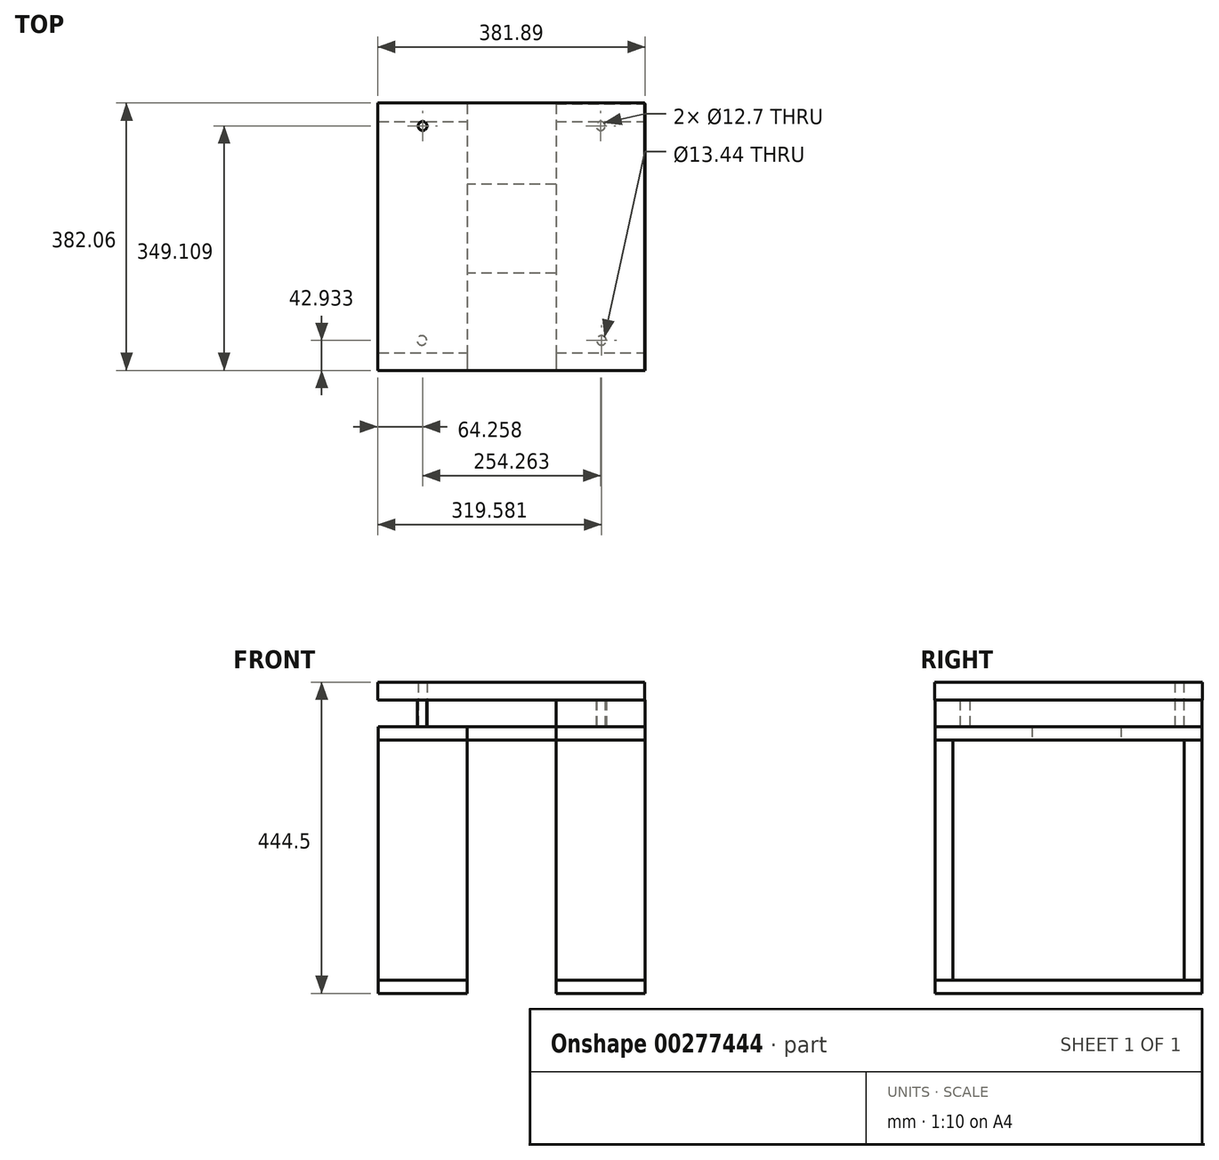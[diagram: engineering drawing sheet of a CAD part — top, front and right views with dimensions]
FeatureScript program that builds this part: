
annotation { "Feature Type Name" : "Feature", "Feature Type Description" : "" }
export const myFeature = defineFeature(function(context is Context, id is Id, definition is map)
    precondition{}
    {
        {
            var Q0;
            Q0=qCreatedBy(makeId("Top.planeOp"),FACE);
            var sketch = newSketch(context, id + "F0", { "sketchPlane" : qUnion([Q0])});
            skLineSegment(sketch, "E0.bottom", {"start": v(63.5, 136.92) * mm, "end": v(190.5, 136.92) * mm});
            skLineSegment(sketch, "E0.top", {"start": v(63.5, -244.08) * mm, "end": v(190.5, -244.08) * mm});
            skLineSegment(sketch, "E0.left", {"start": v(63.5, 136.92) * mm, "end": v(63.5, -244.08) * mm});
            skLineSegment(sketch, "E0.right", {"start": v(190.5, 136.92) * mm, "end": v(190.5, -244.08) * mm});
            skLineSegment(sketch, "E1", {"start": v(0, 353.22) * mm, "end": v(0, -367.1) * mm});
            skLineSegment(sketch, "E2.MirrorCS", {"start": v(-190.5, 136.92) * mm, "end": v(-190.5, -244.08) * mm});
            skLineSegment(sketch, "E3.MirrorCS", {"start": v(-63.5, 136.92) * mm, "end": v(-190.5, 136.92) * mm});
            skLineSegment(sketch, "E4.MirrorCS", {"start": v(-63.5, 136.92) * mm, "end": v(-63.5, -244.08) * mm});
            skLineSegment(sketch, "E5.MirrorCS", {"start": v(-63.5, -244.08) * mm, "end": v(-190.5, -244.08) * mm});
            skSolve(sketch);
        }
        {
            var Q0;
            Q0=makeQuery(id+"F0.imprint","IMPRINT",FACE,{"disambiguationData":[TD([[makeQuery(id+"F0.imprint","IMPRINT",EDGE,{"derivedFrom":sQuery(id+"F0.wireOp",EDGE,"E2.MirrorCS")}),1.0]])]});
            var Q1;
            Q1=makeQuery(id+"F0.imprint","IMPRINT",FACE,{"disambiguationData":[TD([[makeQuery(id+"F0.imprint","IMPRINT",EDGE,{"derivedFrom":sQuery(id+"F0.wireOp",EDGE,"E0.bottom")}),-1.0]])]});
            extrude(context, id + "F1", {"entities" : qUnion([Q0, Q1]), "depth" : 19.05 * mm});
        }
        {
            var Q0;
            Q0=makeQuery(id+"F1.opExtrude","CAP_FACE",FACE,{"disambiguationData":[OSD([sQuery(id+"F0.wireOp",EDGE,"E2.MirrorCS"),sQuery(id+"F0.wireOp",EDGE,"E3.MirrorCS"),sQuery(id+"F0.wireOp",EDGE,"E4.MirrorCS"),sQuery(id+"F0.wireOp",EDGE,"E5.MirrorCS")])],"isStart":false});
            var sketch = newSketch(context, id + "F2", { "sketchPlane" : qUnion([Q0])});
            skLineSegment(sketch, "E6.bottom", {"start": v(-190.5, 136.92) * mm, "end": v(-63.5, 136.92) * mm});
            skLineSegment(sketch, "E6.top", {"start": v(-190.5, 111.52) * mm, "end": v(-63.5, 111.52) * mm});
            skLineSegment(sketch, "E6.left", {"start": v(-190.5, 136.92) * mm, "end": v(-190.5, 111.52) * mm});
            skLineSegment(sketch, "E6.right", {"start": v(-63.5, 136.92) * mm, "end": v(-63.5, 111.52) * mm});
            skLineSegment(sketch, "E7.bottom", {"start": v(63.15, 136.92) * mm, "end": v(190.15, 136.92) * mm});
            skLineSegment(sketch, "E7.top", {"start": v(63.15, 111.52) * mm, "end": v(190.15, 111.52) * mm});
            skLineSegment(sketch, "E7.left", {"start": v(63.15, 136.92) * mm, "end": v(63.15, 111.52) * mm});
            skLineSegment(sketch, "E7.right", {"start": v(190.15, 136.92) * mm, "end": v(190.15, 111.52) * mm});
            skLineSegment(sketch, "E8.bottom", {"start": v(-190.5, -218.68) * mm, "end": v(-63.5, -218.68) * mm});
            skLineSegment(sketch, "E8.top", {"start": v(-190.5, -244.08) * mm, "end": v(-63.5, -244.08) * mm});
            skLineSegment(sketch, "E8.left", {"start": v(-190.5, -218.68) * mm, "end": v(-190.5, -244.08) * mm});
            skLineSegment(sketch, "E8.right", {"start": v(-63.5, -218.68) * mm, "end": v(-63.5, -244.08) * mm});
            skLineSegment(sketch, "E9.bottom", {"start": v(63.15, -218.68) * mm, "end": v(190.15, -218.68) * mm});
            skLineSegment(sketch, "E9.top", {"start": v(63.15, -244.08) * mm, "end": v(190.15, -244.08) * mm});
            skLineSegment(sketch, "E9.left", {"start": v(63.15, -218.68) * mm, "end": v(63.15, -244.08) * mm});
            skLineSegment(sketch, "E9.right", {"start": v(190.15, -218.68) * mm, "end": v(190.15, -244.08) * mm});
            skSolve(sketch);
        }
        {
            var Q0;
            Q0=makeQuery(id+"F2.imprint","IMPRINT",FACE,{"disambiguationData":[TD([[makeQuery(id+"F2.imprint","IMPRINT",EDGE,{"derivedFrom":sQuery(id+"F2.wireOp",EDGE,"E6.bottom")}),1.0]])]});
            var Q1;
            Q1=makeQuery(id+"F2.imprint","IMPRINT",FACE,{"disambiguationData":[TD([[makeQuery(id+"F2.imprint","IMPRINT",EDGE,{"derivedFrom":sQuery(id+"F2.wireOp",EDGE,"E7.bottom")}),-1.0]])]});
            var Q2;
            Q2=makeQuery(id+"F2.imprint","IMPRINT",FACE,{"disambiguationData":[TD([[makeQuery(id+"F2.imprint","IMPRINT",EDGE,{"derivedFrom":sQuery(id+"F2.wireOp",EDGE,"E9.bottom")}),-1.0]])]});
            var Q3;
            Q3=makeQuery(id+"F2.imprint","IMPRINT",FACE,{"disambiguationData":[TD([[makeQuery(id+"F2.imprint","IMPRINT",EDGE,{"derivedFrom":sQuery(id+"F2.wireOp",EDGE,"E8.bottom")}),-1.0]])]});
            extrude(context, id + "F3", {"entities" : qUnion([Q0, Q1, Q2, Q3]), "depth" : 342.9 * mm});
        }
        {
            var Q0;
            Q0=makeQuery(id+"F3.opExtrude","CAP_FACE",FACE,{"disambiguationData":[OSD([sQuery(id+"F2.wireOp",EDGE,"E6.bottom"),sQuery(id+"F2.wireOp",EDGE,"E6.top"),sQuery(id+"F2.wireOp",EDGE,"E6.left"),sQuery(id+"F2.wireOp",EDGE,"E6.right")])],"isStart":false});
            var sketch = newSketch(context, id + "F4", { "sketchPlane" : qUnion([Q0])});
            skLineSegment(sketch, "E10", {"start": v(0, 176.36) * mm, "end": v(0, -297.99) * mm});
            skLineSegment(sketch, "E11.bottom", {"start": v(-190.5, 136.92) * mm, "end": v(-63.5, 136.92) * mm});
            skLineSegment(sketch, "E11.top", {"start": v(-190.5, -244.08) * mm, "end": v(-63.5, -244.08) * mm});
            skLineSegment(sketch, "E11.left", {"start": v(-190.5, 136.92) * mm, "end": v(-190.5, -244.08) * mm});
            skLineSegment(sketch, "E11.right", {"start": v(-63.5, 136.92) * mm, "end": v(-63.5, -244.08) * mm});
            skLineSegment(sketch, "E12.MirrorCS", {"start": v(190.5, 136.92) * mm, "end": v(63.5, 136.92) * mm});
            skLineSegment(sketch, "E13.MirrorCS", {"start": v(190.5, 136.92) * mm, "end": v(190.5, -244.08) * mm});
            skLineSegment(sketch, "E14.MirrorCS", {"start": v(63.5, 136.92) * mm, "end": v(63.5, -244.08) * mm});
            skLineSegment(sketch, "E15.MirrorCS", {"start": v(190.5, -244.08) * mm, "end": v(63.5, -244.08) * mm});
            skSolve(sketch);
        }
        {
            var Q0;
            {var subQ0=sQuery(id+"F4.wireOp",EDGE,"E11.top");Q0=makeQuery(id+"F4.imprint","IMPRINT",FACE,{"disambiguationData":[TD([[makeQuery(id+"F4.imprint","IMPRINT",EDGE,{"derivedFrom":subQ0}),1.0]])]});}
            var Q1;
            {var subQ0=sQuery(id+"F4.wireOp",EDGE,"E11.bottom");Q1=makeQuery(id+"F4.imprint","IMPRINT",FACE,{"disambiguationData":[TD([[makeQuery(id+"F4.imprint","IMPRINT",EDGE,{"derivedFrom":subQ0}),1.0]])]});}
            var Q2;
            Q2=makeQuery(id+"F4.imprint","IMPRINT",FACE,{"disambiguationData":[TD([[makeQuery(id+"F4.imprint","IMPRINT",EDGE,{"derivedFrom":sQuery(id+"F4.wireOp",EDGE,"E12.MirrorCS")}),1.0]])]});
            extrude(context, id + "F5", {"entities" : qUnion([Q0, Q1, Q2]), "depth" : 19.05 * mm});
        }
        {
            var Q0;
            Q0=makeQuery(id+"F5.opExtrude","SWEPT_FACE",FACE,{"disambiguationData":[OSD([sQuery(id+"F4.wireOp",EDGE,"E11.right")])]});
            var sketch = newSketch(context, id + "F6", { "sketchPlane" : qUnion([Q0])});
            skLineSegment(sketch, "E16.bottom", {"start": v(-105.58, 381) * mm, "end": v(21.42, 381) * mm});
            skLineSegment(sketch, "E16.top", {"start": v(-105.58, 361.95) * mm, "end": v(21.42, 361.95) * mm});
            skLineSegment(sketch, "E16.left", {"start": v(-105.58, 381) * mm, "end": v(-105.58, 361.95) * mm});
            skLineSegment(sketch, "E16.right", {"start": v(21.42, 381) * mm, "end": v(21.42, 361.95) * mm});
            skSolve(sketch);
        }
        {
            var Q0;
            Q0=makeQuery(id+"F6.imprint","IMPRINT",FACE,{"disambiguationData":[TD([[makeQuery(id+"F6.imprint","IMPRINT",EDGE,{"derivedFrom":sQuery(id+"F6.wireOp",EDGE,"E16.bottom")}),1.0]])]});
            extrude(context, id + "F7", {"entities" : qUnion([Q0]), "depth" : 127 * mm});
        }
        {
            var Q0;
            Q0=makeQuery(id+"F5.opExtrude","CAP_FACE",FACE,{"disambiguationData":[OSD([sQuery(id+"F4.wireOp",EDGE,"E12.MirrorCS"),sQuery(id+"F4.wireOp",EDGE,"E13.MirrorCS"),sQuery(id+"F4.wireOp",EDGE,"E14.MirrorCS"),sQuery(id+"F4.wireOp",EDGE,"E15.MirrorCS")])],"isStart":false});
            var sketch = newSketch(context, id + "F8", { "sketchPlane" : qUnion([Q0])});
            skLineSegment(sketch, "E17", {"start": v(0, 100.66) * mm, "end": v(0, -211.53) * mm});
            skCircle(sketch, "E18", {"center": v(-127.13, 104.86) * mm, "radius": 6.35 * mm});
            skCircle(sketch, "E19", {"center": v(-128.2, -201.32) * mm, "radius": 6.72 * mm});
            skCircle(sketch, "E20.MirrorC", {"center": v(127.13, 104.86) * mm, "radius": 6.35 * mm});
            skCircle(sketch, "E21.MirrorC", {"center": v(128.2, -201.32) * mm, "radius": 6.72 * mm});
            skSolve(sketch);
        }
        {
            var Q0;
            Q0=makeQuery(id+"F8.imprint","IMPRINT",FACE,{"disambiguationData":[TD([[makeQuery(id+"F8.imprint","IMPRINT",EDGE,{"derivedFrom":sQuery(id+"F8.wireOp",EDGE,"E18")}),1.0]])]});
            var Q1;
            Q1=makeQuery(id+"F8.imprint","IMPRINT",FACE,{"disambiguationData":[TD([[makeQuery(id+"F8.imprint","IMPRINT",EDGE,{"derivedFrom":sQuery(id+"F8.wireOp",EDGE,"E20.MirrorC")}),-1.0]])]});
            var Q2;
            Q2=makeQuery(id+"F8.imprint","IMPRINT",FACE,{"disambiguationData":[TD([[makeQuery(id+"F8.imprint","IMPRINT",EDGE,{"derivedFrom":sQuery(id+"F8.wireOp",EDGE,"E19")}),1.0]])]});
            var Q3;
            Q3=makeQuery(id+"F8.imprint","IMPRINT",FACE,{"disambiguationData":[TD([[makeQuery(id+"F8.imprint","IMPRINT",EDGE,{"derivedFrom":sQuery(id+"F8.wireOp",EDGE,"E21.MirrorC")}),-1.0]])]});
            extrude(context, id + "F9", {"entities" : qUnion([Q0, Q1, Q2, Q3]), "depth" : 38.1 * mm});
        }
        {
            var Q0;
            Q0=makeQuery(id+"F9.opExtrude","CAP_FACE",FACE,{"disambiguationData":[OSD([sQuery(id+"F8.wireOp",EDGE,"E18")])],"isStart":false});
            var sketch = newSketch(context, id + "F10", { "sketchPlane" : qUnion([Q0])});
            skLineSegment(sketch, "E22.bottom", {"start": v(-191.4, 137.81) * mm, "end": v(189.95, 137.81) * mm});
            skLineSegment(sketch, "E22.top", {"start": v(-191.4, -244.25) * mm, "end": v(189.95, -244.25) * mm});
            skLineSegment(sketch, "E22.left", {"start": v(-191.4, 137.81) * mm, "end": v(-191.4, -244.25) * mm});
            skLineSegment(sketch, "E22.right", {"start": v(189.95, 137.81) * mm, "end": v(189.95, -244.25) * mm});
            skSolve(sketch);
        }
        {
            var Q0;
            Q0=makeQuery(id+"F10.imprint","IMPRINT",FACE,{"disambiguationData":[TD([[makeQuery(id+"F10.imprint","IMPRINT",EDGE,{"derivedFrom":sQuery(id+"F10.wireOp",EDGE,"E22.bottom")}),-1.0]])]});
            extrude(context, id + "F11", {"entities" : qUnion([Q0]), "depth" : 25.4 * mm});
        }
    });
